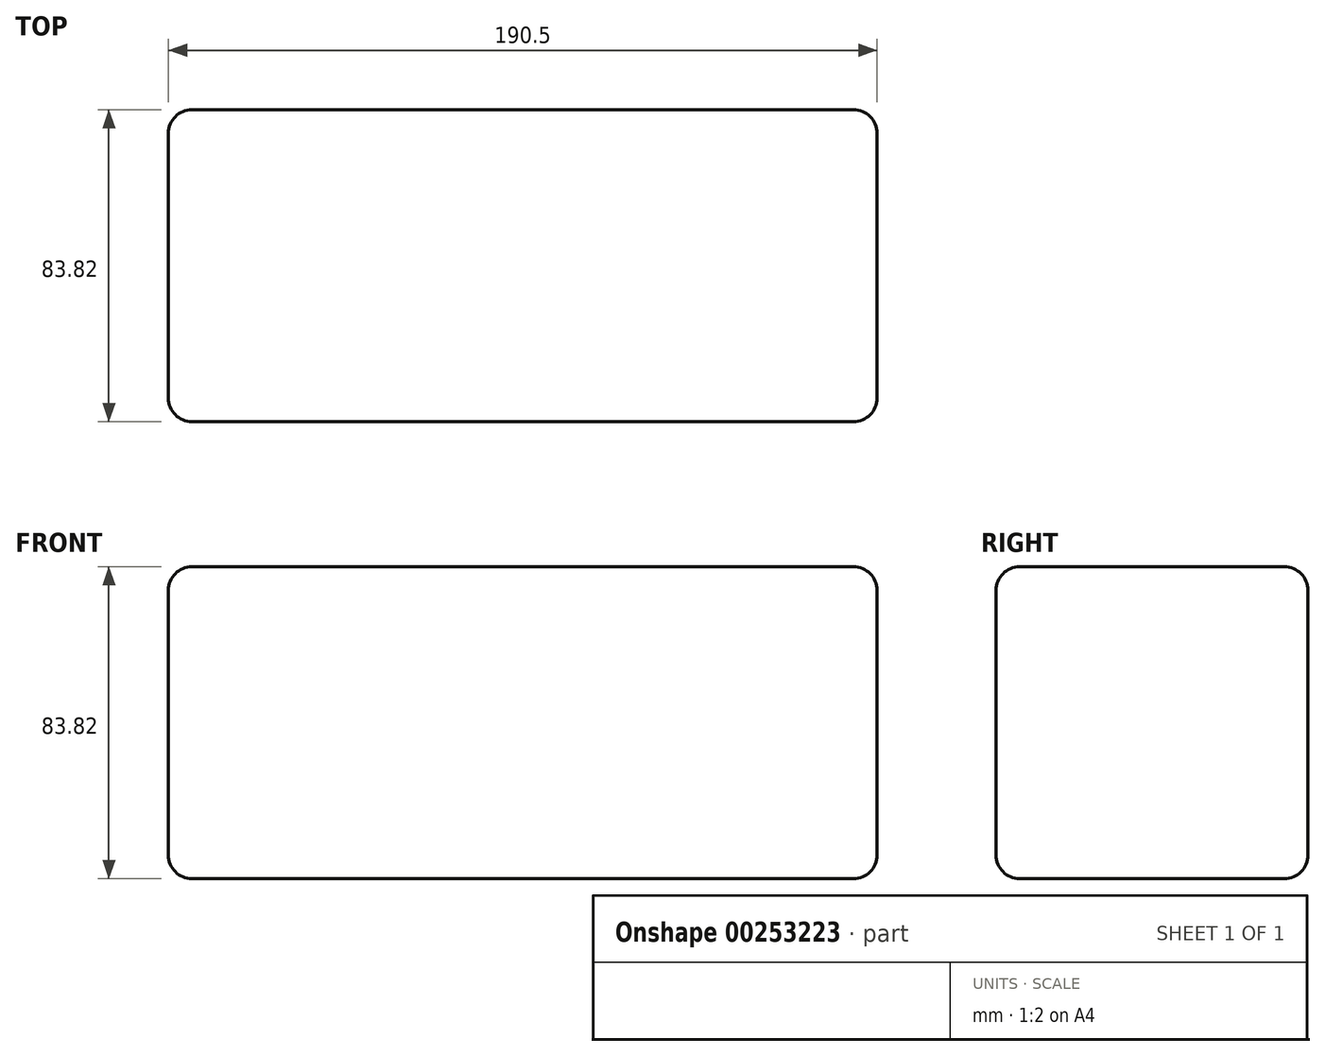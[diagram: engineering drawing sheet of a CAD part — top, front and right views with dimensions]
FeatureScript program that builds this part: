
annotation { "Feature Type Name" : "Feature", "Feature Type Description" : "" }
export const myFeature = defineFeature(function(context is Context, id is Id, definition is map)
    precondition{}
    {
        {
            var Q0;
            Q0=qCreatedBy(makeId("Top.planeOp"),FACE);
            var sketch = newSketch(context, id + "F0", { "sketchPlane" : qUnion([Q0])});
            skLineSegment(sketch, "E0.bottom", {"start": v(0, 0) * mm, "end": v(190.5, 0) * mm});
            skLineSegment(sketch, "E0.top", {"start": v(0, 83.82) * mm, "end": v(190.5, 83.82) * mm});
            skLineSegment(sketch, "E0.left", {"start": v(0, 0) * mm, "end": v(0, 83.82) * mm});
            skLineSegment(sketch, "E0.right", {"start": v(190.5, 0) * mm, "end": v(190.5, 83.82) * mm});
            skSolve(sketch);
        }
        {
            var Q0;
            Q0 = qSketchRegion(id + "F0", true);
            extrude(context, id + "F1", {"entities" : qUnion([Q0]), "depth" : 83.82 * mm});
        }
        {
            var Q0;
            Q0=makeQuery(id+"F1.opExtrude","CAP_EDGE",EDGE,{"disambiguationData":[OSD([sQuery(id+"F0.wireOp",EDGE,"E0.bottom")])],"isStart":false});
            var Q1;
            Q1=makeQuery(id+"F1.opExtrude","CAP_EDGE",EDGE,{"disambiguationData":[OSD([sQuery(id+"F0.wireOp",EDGE,"E0.left")])],"isStart":false});
            var Q2;
            Q2=makeQuery(id+"F1.opExtrude","CAP_EDGE",EDGE,{"disambiguationData":[OSD([sQuery(id+"F0.wireOp",EDGE,"E0.top")])],"isStart":false});
            var Q3;
            Q3=makeQuery(id+"F1.opExtrude","CAP_EDGE",EDGE,{"disambiguationData":[OSD([sQuery(id+"F0.wireOp",EDGE,"E0.right")])],"isStart":false});
            var Q4;
            Q4=makeQuery(id+"F1.opExtrude","SWEPT_EDGE",EDGE,{"disambiguationData":[OSD([sQuery(id+"F0.wireOp",EDGE,"E0.bottom"),sQuery(id+"F0.wireOp",EDGE,"E0.right")])]});
            var Q5;
            Q5=makeQuery(id+"F1.opExtrude","CAP_EDGE",EDGE,{"disambiguationData":[OSD([sQuery(id+"F0.wireOp",EDGE,"E0.bottom")])],"isStart":true});
            var Q6;
            Q6=makeQuery(id+"F1.opExtrude","CAP_EDGE",EDGE,{"disambiguationData":[OSD([sQuery(id+"F0.wireOp",EDGE,"E0.right")])],"isStart":true});
            var Q7;
            Q7=makeQuery(id+"F1.opExtrude","SWEPT_EDGE",EDGE,{"disambiguationData":[OSD([sQuery(id+"F0.wireOp",EDGE,"E0.bottom"),sQuery(id+"F0.wireOp",EDGE,"E0.left")])]});
            var Q8;
            Q8=makeQuery(id+"F1.opExtrude","SWEPT_EDGE",EDGE,{"disambiguationData":[OSD([sQuery(id+"F0.wireOp",EDGE,"E0.top"),sQuery(id+"F0.wireOp",EDGE,"E0.left")])]});
            var Q9;
            Q9=makeQuery(id+"F1.opExtrude","CAP_EDGE",EDGE,{"disambiguationData":[OSD([sQuery(id+"F0.wireOp",EDGE,"E0.left")])],"isStart":true});
            var Q10;
            Q10=makeQuery(id+"F1.opExtrude","CAP_EDGE",EDGE,{"disambiguationData":[OSD([sQuery(id+"F0.wireOp",EDGE,"E0.top")])],"isStart":true});
            var Q11;
            Q11=makeQuery(id+"F1.opExtrude","SWEPT_EDGE",EDGE,{"disambiguationData":[OSD([sQuery(id+"F0.wireOp",EDGE,"E0.top"),sQuery(id+"F0.wireOp",EDGE,"E0.right")])]});
            fillet(context, id + "F2", {"entities" : qUnion([Q0, Q1, Q2, Q3, Q4, Q5, Q6, Q7, Q8, Q9, Q10, Q11]), "radius" : 6.35 * mm, "tangentPropagation" : true, "allowEdgeOverflow" : false});
        }
    });
